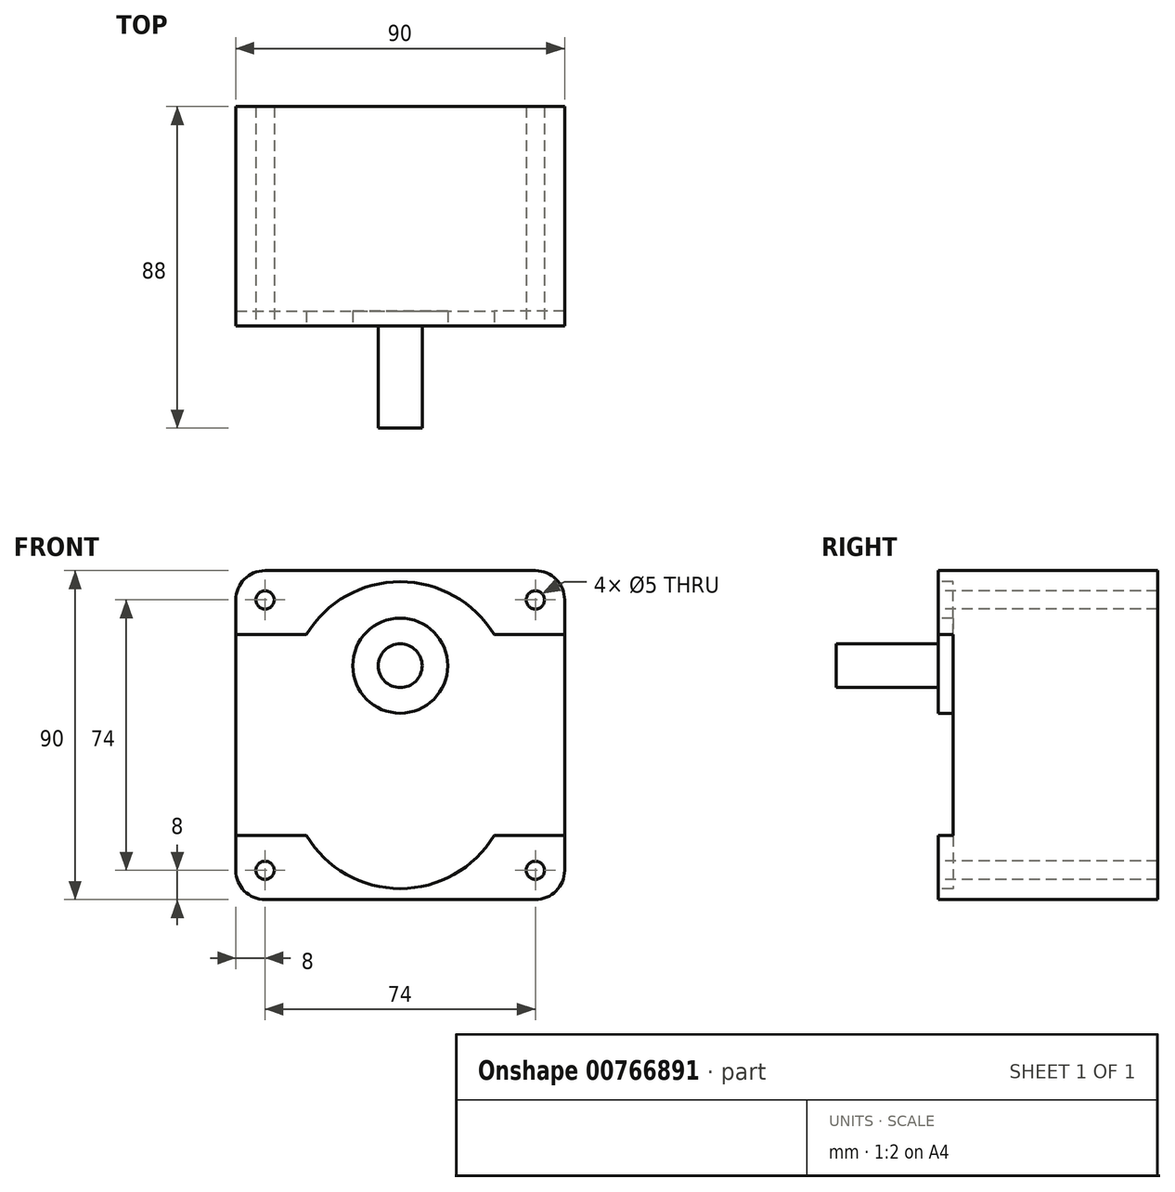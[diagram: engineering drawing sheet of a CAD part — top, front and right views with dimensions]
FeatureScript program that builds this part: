
annotation { "Feature Type Name" : "Feature", "Feature Type Description" : "" }
export const myFeature = defineFeature(function(context is Context, id is Id, definition is map)
    precondition{}
    {
        {
            var Q0;
            Q0=qCreatedBy(makeId("Front.planeOp"),FACE);
            var sketch = newSketch(context, id + "F0", { "sketchPlane" : qUnion([Q0])});
            skLineSegment(sketch, "E0.bottom", {"start": v(-45, -45) * mm, "end": v(45, -45) * mm});
            skLineSegment(sketch, "E0.top", {"start": v(-45, 45) * mm, "end": v(45, 45) * mm});
            skLineSegment(sketch, "E0.left", {"start": v(-45, -45) * mm, "end": v(-45, 45) * mm});
            skLineSegment(sketch, "E0.right", {"start": v(45, -45) * mm, "end": v(45, 45) * mm});
            skSolve(sketch);
        }
        {
            var Q0;
            Q0=makeQuery(id+"F0.imprint","IMPRINT",FACE,{"disambiguationData":[TD([[makeQuery(id+"F0.imprint","IMPRINT",EDGE,{"derivedFrom":sQuery(id+"F0.wireOp",EDGE,"E0.bottom")}),1.0]])]});
            extrude(context, id + "F1", {"entities" : qUnion([Q0]), "depth" : 30 * mm, "offsetDistance" : 25 * mm, "hasSecondDirection" : true, "secondDirectionOppositeDirection" : true, "secondDirectionDepth" : 30 * mm});
        }
        {
            var Q0;
            Q0=makeQuery(id+"F1.opExtrude","CAP_FACE",FACE,{"disambiguationData":[OSD([sQuery(id+"F0.wireOp",EDGE,"E0.bottom"),sQuery(id+"F0.wireOp",EDGE,"E0.top"),sQuery(id+"F0.wireOp",EDGE,"E0.left"),sQuery(id+"F0.wireOp",EDGE,"E0.right")])],"isStart":false});
            var sketch = newSketch(context, id + "F2", { "sketchPlane" : qUnion([Q0])});
            skLineSegment(sketch, "E1.0", {"start": v(-45, 45) * mm, "end": v(45, 45) * mm});
            skLineSegment(sketch, "E2.0", {"start": v(-45, -45) * mm, "end": v(-45, 45) * mm});
            skLineSegment(sketch, "E3.0", {"start": v(-45, -45) * mm, "end": v(45, -45) * mm});
            skLineSegment(sketch, "E4.0", {"start": v(45, -45) * mm, "end": v(45, 45) * mm});
            skArc(sketch, "E5", {"start": v(25.69, 27.5) * mm, "mid": v(0, 42) * mm, "end": v(-25.69, 27.5) * mm});
            skArc(sketch, "E6", {"start": v(-25.69, -27.5) * mm, "mid": v(0, -42) * mm, "end": v(25.69, -27.5) * mm});
            skCircle(sketch, "E7", {"center": v(-37, 37) * mm, "radius": 2.5 * mm});
            skCircle(sketch, "E8", {"center": v(-37, -37) * mm, "radius": 2.5 * mm});
            skCircle(sketch, "E9", {"center": v(37, -37) * mm, "radius": 2.5 * mm});
            skCircle(sketch, "E10", {"center": v(37, 37) * mm, "radius": 2.5 * mm});
            skLineSegment(sketch, "E11", {"start": v(-45, 27.5) * mm, "end": v(-25.69, 27.5) * mm});
            skLineSegment(sketch, "E12", {"start": v(45, -27.5) * mm, "end": v(25.69, -27.5) * mm});
            skLineSegment(sketch, "E13.trimOffspring", {"start": v(25.69, 27.5) * mm, "end": v(45, 27.5) * mm});
            skLineSegment(sketch, "E14.trimOffspring", {"start": v(-25.69, -27.5) * mm, "end": v(-45, -27.5) * mm});
            skCircle(sketch, "E15", {"center": v(0, 19) * mm, "radius": 13 * mm});
            skCircle(sketch, "E16", {"center": v(0, 19) * mm, "radius": 6 * mm});
            skSolve(sketch);
        }
        {
            var Q0;
            Q0=makeQuery(id+"F2.imprint","IMPRINT",FACE,{"disambiguationData":[TD([[makeQuery(id+"F2.imprint","IMPRINT",EDGE,{"derivedFrom":sQuery(id+"F2.wireOp",EDGE,"E5")}),1.0]])]});
            extrude(context, id + "F3", {"entities" : qUnion([Q0]), "operationType" : NewBodyOperationType.REMOVE, "oppositeDirection" : true, "depth" : 4 * mm, "offsetDistance" : 25 * mm});
        }
        {
            var Q0;
            Q0=makeQuery(id+"F2.imprint","IMPRINT",FACE,{"disambiguationData":[TD([[makeQuery(id+"F2.imprint","IMPRINT",EDGE,{"derivedFrom":sQuery(id+"F2.wireOp",EDGE,"E7")}),1.0]])]});
            var Q1;
            Q1=makeQuery(id+"F2.imprint","IMPRINT",FACE,{"disambiguationData":[TD([[makeQuery(id+"F2.imprint","IMPRINT",EDGE,{"derivedFrom":sQuery(id+"F2.wireOp",EDGE,"E10")}),1.0]])]});
            var Q2;
            Q2=makeQuery(id+"F2.imprint","IMPRINT",FACE,{"disambiguationData":[TD([[makeQuery(id+"F2.imprint","IMPRINT",EDGE,{"derivedFrom":sQuery(id+"F2.wireOp",EDGE,"E9")}),1.0]])]});
            var Q3;
            Q3=makeQuery(id+"F2.imprint","IMPRINT",FACE,{"disambiguationData":[TD([[makeQuery(id+"F2.imprint","IMPRINT",EDGE,{"derivedFrom":sQuery(id+"F2.wireOp",EDGE,"E8")}),1.0]])]});
            extrude(context, id + "F4", {"entities" : qUnion([Q0, Q1, Q2, Q3]), "operationType" : NewBodyOperationType.REMOVE, "oppositeDirection" : true, "depth" : 60 * mm, "offsetDistance" : 25 * mm});
        }
        {
            var Q0;
            Q0=makeQuery(id+"F2.imprint","IMPRINT",FACE,{"disambiguationData":[TD([[makeQuery(id+"F2.imprint","IMPRINT",EDGE,{"derivedFrom":sQuery(id+"F2.wireOp",EDGE,"E16")}),1.0]])]});
            extrude(context, id + "F5", {"entities" : qUnion([Q0]), "operationType" : NewBodyOperationType.ADD, "depth" : 28 * mm, "offsetDistance" : 25 * mm});
        }
        {
            var Q0;
            Q0=makeQuery(id+"F1.opExtrude","SWEPT_EDGE",EDGE,{"disambiguationData":[OSD([sQuery(id+"F0.wireOp",EDGE,"E0.top"),sQuery(id+"F0.wireOp",EDGE,"E0.right")])]});
            var Q1;
            Q1=makeQuery(id+"F1.opExtrude","SWEPT_EDGE",EDGE,{"disambiguationData":[OSD([sQuery(id+"F0.wireOp",EDGE,"E0.bottom"),sQuery(id+"F0.wireOp",EDGE,"E0.right")])]});
            var Q2;
            Q2=makeQuery(id+"F1.opExtrude","SWEPT_EDGE",EDGE,{"disambiguationData":[OSD([sQuery(id+"F0.wireOp",EDGE,"E0.bottom"),sQuery(id+"F0.wireOp",EDGE,"E0.left")])]});
            var Q3;
            Q3=makeQuery(id+"F1.opExtrude","SWEPT_EDGE",EDGE,{"disambiguationData":[OSD([sQuery(id+"F0.wireOp",EDGE,"E0.top"),sQuery(id+"F0.wireOp",EDGE,"E0.left")])]});
            fillet(context, id + "F6", {"entities" : qUnion([Q0, Q1, Q2, Q3]), "radius" : 8 * mm, "tangentPropagation" : true, "allowEdgeOverflow" : false});
        }
    });
